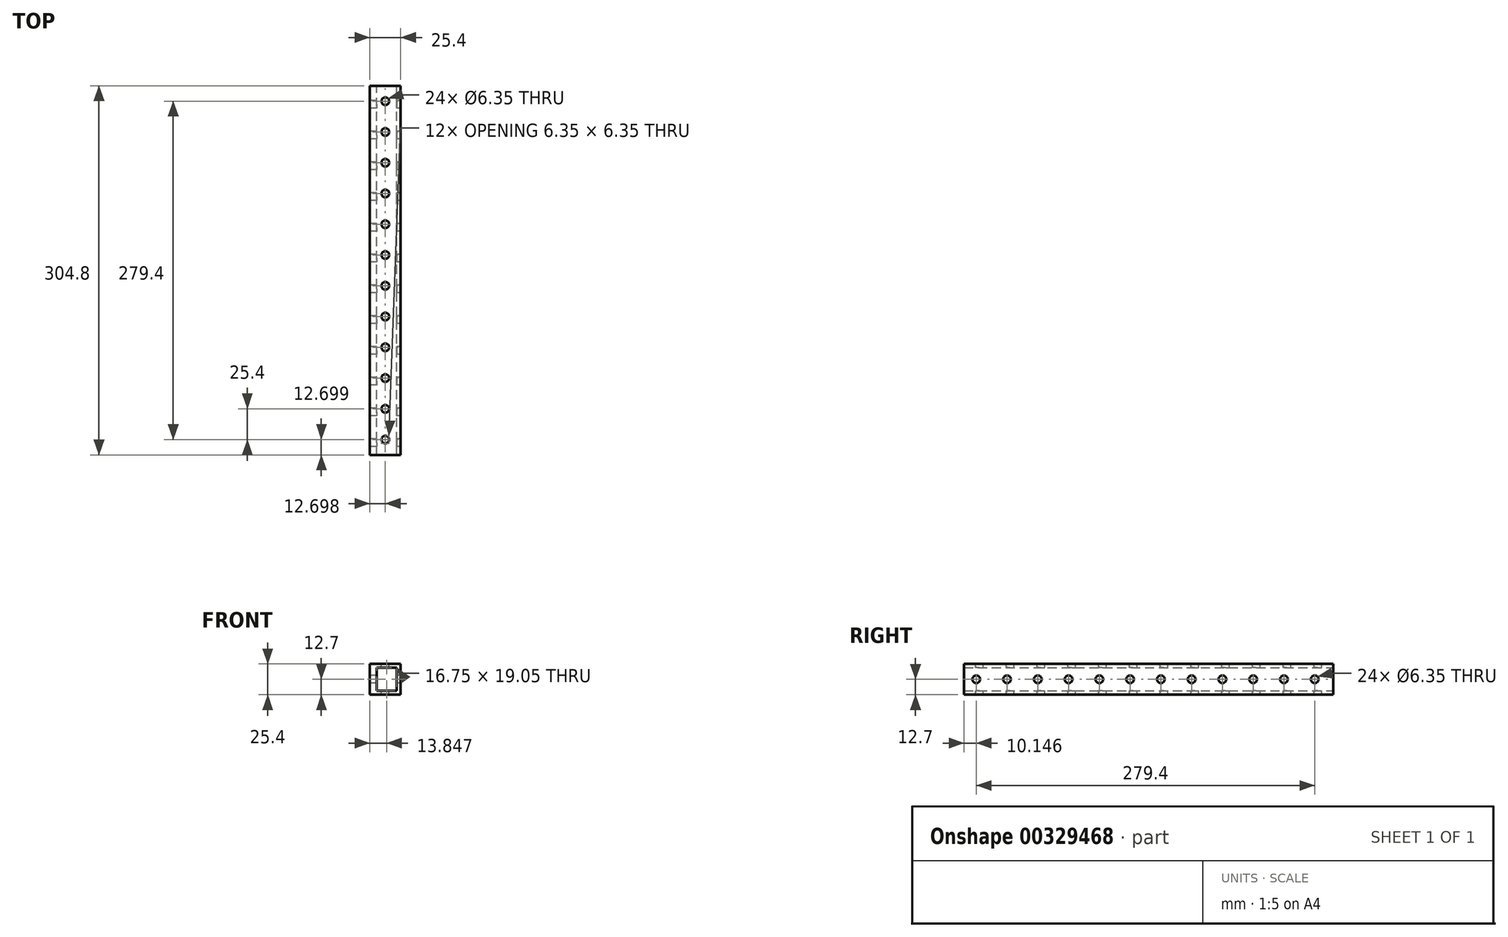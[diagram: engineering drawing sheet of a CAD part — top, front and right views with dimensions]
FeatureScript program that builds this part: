
annotation { "Feature Type Name" : "Feature", "Feature Type Description" : "" }
export const myFeature = defineFeature(function(context is Context, id is Id, definition is map)
    precondition{}
    {
        {
            var Q0;
            Q0=qCreatedBy(makeId("Top.planeOp"),FACE);
            var sketch = newSketch(context, id + "F0", { "sketchPlane" : qUnion([Q0])});
            skLineSegment(sketch, "E0.bottom", {"start": v(-5.47, 287.23) * mm, "end": v(19.93, 287.23) * mm});
            skLineSegment(sketch, "E0.top", {"start": v(-5.47, -17.57) * mm, "end": v(19.93, -17.57) * mm});
            skLineSegment(sketch, "E0.left", {"start": v(-5.47, 287.23) * mm, "end": v(-5.47, -17.57) * mm});
            skLineSegment(sketch, "E0.right", {"start": v(19.93, 287.23) * mm, "end": v(19.93, -17.57) * mm});
            skSolve(sketch);
        }
        {
            var Q0;
            Q0=makeQuery(id+"F0.imprint","IMPRINT",FACE,{"disambiguationData":[TD([[makeQuery(id+"F0.imprint","IMPRINT",EDGE,{"derivedFrom":sQuery(id+"F0.wireOp",EDGE,"E0.bottom")}),-1.0]])]});
            extrude(context, id + "F1", {"entities" : qUnion([Q0]), "depth" : 25.4 * mm});
        }
        {
            var Q0;
            Q0=makeQuery(id+"F1.opExtrude","SWEPT_FACE",FACE,{"disambiguationData":[OSD([sQuery(id+"F0.wireOp",EDGE,"E0.bottom")])]});
            var sketch = newSketch(context, id + "F2", { "sketchPlane" : qUnion([Q0])});
            skLineSegment(sketch, "E1.bottom", {"start": v(-16.75, 22.23) * mm, "end": v(0, 22.23) * mm});
            skLineSegment(sketch, "E1.top", {"start": v(-16.75, 3.18) * mm, "end": v(0, 3.18) * mm});
            skLineSegment(sketch, "E1.left", {"start": v(-16.75, 22.23) * mm, "end": v(-16.75, 3.18) * mm});
            skLineSegment(sketch, "E1.right", {"start": v(0, 22.23) * mm, "end": v(0, 3.18) * mm});
            skSolve(sketch);
        }
        {
            var Q0;
            Q0=makeQuery(id+"F2.imprint","IMPRINT",FACE,{"disambiguationData":[TD([[makeQuery(id+"F2.imprint","IMPRINT",EDGE,{"derivedFrom":sQuery(id+"F2.wireOp",EDGE,"E1.bottom")}),-1.0]])]});
            extrude(context, id + "F3", {"entities" : qUnion([Q0]), "operationType" : NewBodyOperationType.REMOVE, "oppositeDirection" : true, "depth" : 304.8 * mm});
        }
        {
            var Q0;
            Q0=makeQuery(id+"F1.opExtrude","SWEPT_FACE",FACE,{"disambiguationData":[OSD([sQuery(id+"F0.wireOp",EDGE,"E0.left")])]});
            var sketch = newSketch(context, id + "F4", { "sketchPlane" : qUnion([Q0])});
            skCircle(sketch, "E2", {"center": v(-271.98, 12.7) * mm, "radius": 2.55 * mm});
            skCircle(sketch, "E3.1.0.0", {"center": v(-246.58, 12.7) * mm, "radius": 2.55 * mm});
            skCircle(sketch, "E3.2.0.0", {"center": v(-221.18, 12.7) * mm, "radius": 2.55 * mm});
            skCircle(sketch, "E3.3.0.0", {"center": v(-195.78, 12.7) * mm, "radius": 2.55 * mm});
            skCircle(sketch, "E3.4.0.0", {"center": v(-170.38, 12.7) * mm, "radius": 2.55 * mm});
            skCircle(sketch, "E3.5.0.0", {"center": v(-144.98, 12.7) * mm, "radius": 2.55 * mm});
            skCircle(sketch, "E3.6.0.0", {"center": v(-119.58, 12.7) * mm, "radius": 2.55 * mm});
            skCircle(sketch, "E3.7.0.0", {"center": v(-94.18, 12.7) * mm, "radius": 2.55 * mm});
            skCircle(sketch, "E3.8.0.0", {"center": v(-68.78, 12.7) * mm, "radius": 2.55 * mm});
            skCircle(sketch, "E3.9.0.0", {"center": v(-43.38, 12.7) * mm, "radius": 2.55 * mm});
            skCircle(sketch, "E3.10.0.0", {"center": v(-17.98, 12.7) * mm, "radius": 2.55 * mm});
            skLineSegment(sketch, "E3.direction1", {"start": v(-271.98, 12.7) * mm, "end": v(-246.58, 12.7) * mm, "construction": true});
            skCircle(sketch, "E4.0.11.0", {"center": v(7.42, 12.7) * mm, "radius": 2.55 * mm});
            skSolve(sketch);
        }
        {
            var Q0;
            Q0=sQuery(id+"F4.wireOp",VERTEX,"E3.direction1.start");
            var Q1;
            Q1=sQuery(id+"F4.wireOp",VERTEX,"E3.10.0.0.center");
            var Q2;
            Q2=sQuery(id+"F4.wireOp",VERTEX,"E3.9.0.0.center");
            var Q3;
            Q3=sQuery(id+"F4.wireOp",VERTEX,"E3.8.0.0.center");
            var Q4;
            Q4=sQuery(id+"F4.wireOp",VERTEX,"E3.7.0.0.center");
            var Q5;
            Q5=sQuery(id+"F4.wireOp",VERTEX,"E3.6.0.0.center");
            var Q6;
            Q6=sQuery(id+"F4.wireOp",VERTEX,"E3.5.0.0.center");
            var Q7;
            Q7=sQuery(id+"F4.wireOp",VERTEX,"E3.4.0.0.center");
            var Q8;
            Q8=sQuery(id+"F4.wireOp",VERTEX,"E3.3.0.0.center");
            var Q9;
            Q9=sQuery(id+"F4.wireOp",VERTEX,"E3.2.0.0.center");
            var Q10;
            Q10=sQuery(id+"F4.wireOp",VERTEX,"E3.1.0.0.center");
            var Q11;
            Q11=sQuery(id+"F4.wireOp",VERTEX,"E4.0.11.0.center");
            var Q12;
            Q12=makeQuery(id+"F1.opExtrude","SWEPT_BODY",BODY,{"disambiguationData":[OSD([sQuery(id+"F0.wireOp",EDGE,"E0.bottom"),sQuery(id+"F0.wireOp",EDGE,"E0.top"),sQuery(id+"F0.wireOp",EDGE,"E0.left"),sQuery(id+"F0.wireOp",EDGE,"E0.right")])]});
            hole(context, id + "F5", {"style" : HoleStyle.SIMPLE, "endStyle" : HoleEndStyle.THROUGH, "holeDiameter" : 6.35 * mm, "tappedDepth" : 12.7 * mm, "tapClearance" : 3, "locations" : qUnion([Q0, Q1, Q2, Q3, Q4, Q5, Q6, Q7, Q8, Q9, Q10, Q11]), "scope" : qUnion([Q12])});
        }
        {
            var Q0;
            Q0=makeQuery(id+"F1.opExtrude","CAP_FACE",FACE,{"disambiguationData":[OSD([sQuery(id+"F0.wireOp",EDGE,"E0.bottom"),sQuery(id+"F0.wireOp",EDGE,"E0.top"),sQuery(id+"F0.wireOp",EDGE,"E0.left"),sQuery(id+"F0.wireOp",EDGE,"E0.right")])],"isStart":false});
            var sketch = newSketch(context, id + "F6", { "sketchPlane" : qUnion([Q0])});
            skCircle(sketch, "E5", {"center": v(7.23, 274.53) * mm, "radius": 2.55 * mm});
            skCircle(sketch, "E6.0.1.0", {"center": v(7.23, 249.13) * mm, "radius": 2.55 * mm});
            skCircle(sketch, "E6.0.2.0", {"center": v(7.23, 223.73) * mm, "radius": 2.55 * mm});
            skCircle(sketch, "E6.0.3.0", {"center": v(7.23, 198.33) * mm, "radius": 2.55 * mm});
            skCircle(sketch, "E6.0.4.0", {"center": v(7.23, 172.93) * mm, "radius": 2.55 * mm});
            skCircle(sketch, "E6.0.5.0", {"center": v(7.23, 147.53) * mm, "radius": 2.55 * mm});
            skCircle(sketch, "E6.0.6.0", {"center": v(7.23, 122.13) * mm, "radius": 2.55 * mm});
            skCircle(sketch, "E6.0.7.0", {"center": v(7.23, 96.73) * mm, "radius": 2.55 * mm});
            skCircle(sketch, "E6.0.8.0", {"center": v(7.23, 71.33) * mm, "radius": 2.55 * mm});
            skCircle(sketch, "E6.0.9.0", {"center": v(7.23, 45.93) * mm, "radius": 2.55 * mm});
            skCircle(sketch, "E6.0.10.0", {"center": v(7.23, 20.53) * mm, "radius": 2.55 * mm});
            skCircle(sketch, "E6.0.11.0", {"center": v(7.23, -4.87) * mm, "radius": 2.55 * mm});
            skLineSegment(sketch, "E6.direction1", {"start": v(7.23, 274.53) * mm, "end": v(32.63, 274.53) * mm, "construction": true});
            skLineSegment(sketch, "E6.direction2", {"start": v(7.23, 274.53) * mm, "end": v(7.23, 249.13) * mm, "construction": true});
            skSolve(sketch);
        }
        {
            var Q0;
            Q0=sQuery(id+"F6.wireOp",VERTEX,"E6.0.9.0.center");
            var Q1;
            Q1=sQuery(id+"F6.wireOp",VERTEX,"E6.0.10.0.center");
            var Q2;
            Q2=sQuery(id+"F6.wireOp",VERTEX,"E6.0.11.0.center");
            var Q3;
            Q3=sQuery(id+"F6.wireOp",VERTEX,"E6.0.5.0.center");
            var Q4;
            Q4=sQuery(id+"F6.wireOp",VERTEX,"E6.0.4.0.center");
            var Q5;
            Q5=sQuery(id+"F6.wireOp",VERTEX,"E6.0.7.0.center");
            var Q6;
            Q6=sQuery(id+"F6.wireOp",VERTEX,"E6.0.6.0.center");
            var Q7;
            Q7=sQuery(id+"F6.wireOp",VERTEX,"E6.0.8.0.center");
            var Q8;
            Q8=sQuery(id+"F6.wireOp",VERTEX,"E6.0.1.0.center");
            var Q9;
            Q9=sQuery(id+"F6.wireOp",VERTEX,"E5.center");
            var Q10;
            Q10=sQuery(id+"F6.wireOp",VERTEX,"E6.0.2.0.center");
            var Q11;
            Q11=sQuery(id+"F6.wireOp",VERTEX,"E6.0.3.0.center");
            var Q12;
            Q12=makeQuery(id+"F1.opExtrude","SWEPT_BODY",BODY,{"disambiguationData":[OSD([sQuery(id+"F0.wireOp",EDGE,"E0.bottom"),sQuery(id+"F0.wireOp",EDGE,"E0.top"),sQuery(id+"F0.wireOp",EDGE,"E0.left"),sQuery(id+"F0.wireOp",EDGE,"E0.right")])]});
            hole(context, id + "F7", {"style" : HoleStyle.SIMPLE, "endStyle" : HoleEndStyle.THROUGH, "holeDiameter" : 6.35 * mm, "tappedDepth" : 12.7 * mm, "tapClearance" : 3, "locations" : qUnion([Q0, Q1, Q2, Q3, Q4, Q5, Q6, Q7, Q8, Q9, Q10, Q11]), "scope" : qUnion([Q12])});
        }
    });
